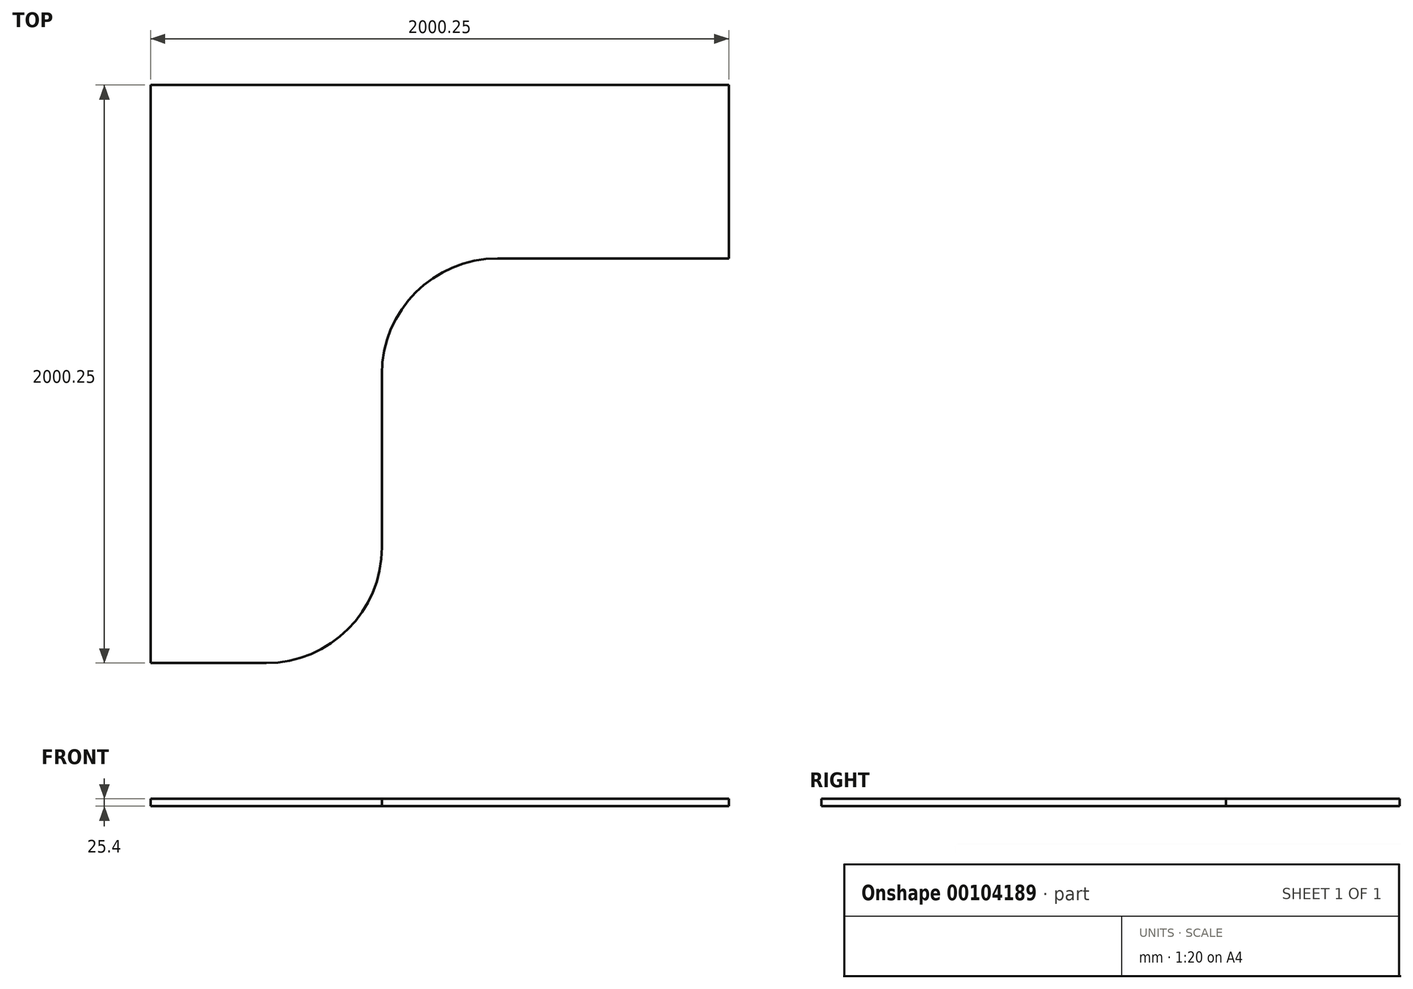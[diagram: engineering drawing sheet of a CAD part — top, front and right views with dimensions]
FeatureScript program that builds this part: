
annotation { "Feature Type Name" : "Feature", "Feature Type Description" : "" }
export const myFeature = defineFeature(function(context is Context, id is Id, definition is map)
    precondition{}
    {
        {
            var Q0;
            Q0=qCreatedBy(makeId("Top.planeOp"),FACE);
            var sketch = newSketch(context, id + "F0", { "sketchPlane" : qUnion([Q0])});
            skLineSegment(sketch, "E0", {"start": v(0, 0) * mm, "end": v(2000.25, 0) * mm});
            skLineSegment(sketch, "E1", {"start": v(2000.25, 0) * mm, "end": v(2000.25, -600.07) * mm});
            skLineSegment(sketch, "E2", {"start": v(2000.25, -600.08) * mm, "end": v(1200.15, -600.08) * mm});
            skLineSegment(sketch, "E3", {"start": v(0, 0) * mm, "end": v(0, -2000.25) * mm});
            skLineSegment(sketch, "E4", {"start": v(0, -2000.25) * mm, "end": v(400.05, -2000.25) * mm});
            skArc(sketch, "E5", {"start": v(400.05, -2000.25) * mm, "mid": v(682.93, -1883.08) * mm, "end": v(800.1, -1600.2) * mm});
            skArc(sketch, "E6", {"start": v(1200.15, -600.08) * mm, "mid": v(917.27, -717.25) * mm, "end": v(800.1, -1000.13) * mm});
            skLineSegment(sketch, "E7", {"start": v(800.1, -1600.2) * mm, "end": v(800.1, -1000.13) * mm});
            skSolve(sketch);
        }
        {
            var Q0;
            Q0=qSketchRegion(id+"F0",true);
            extrude(context, id + "F1", {"entities" : qUnion([Q0]), "oppositeDirection" : true, "depth" : 25.4 * mm});
        }
    });
